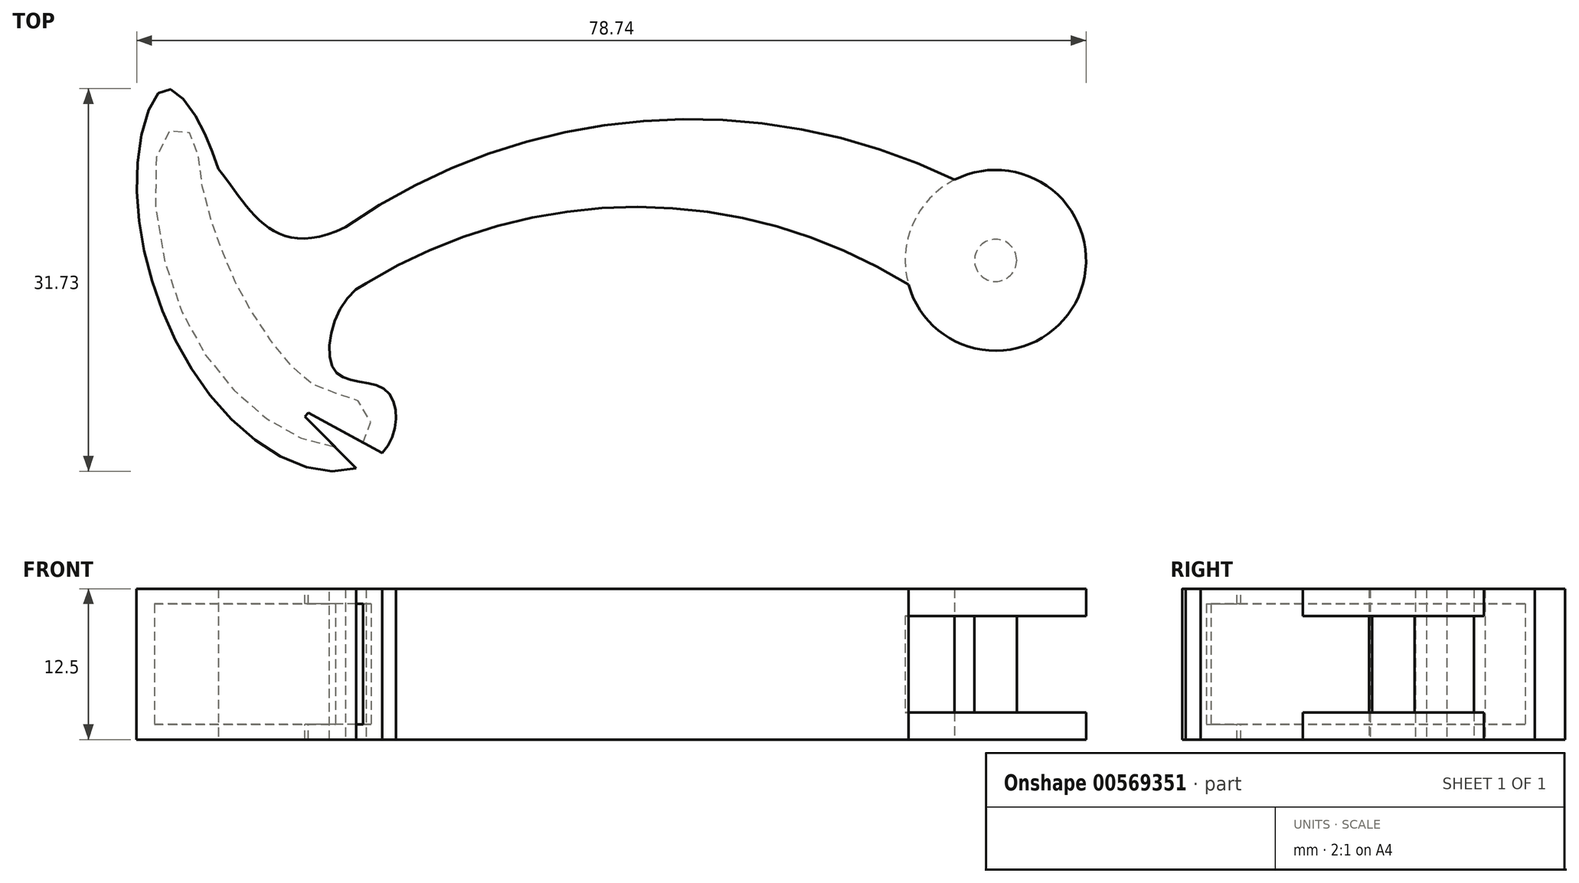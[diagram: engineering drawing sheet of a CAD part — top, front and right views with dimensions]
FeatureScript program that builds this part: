
annotation { "Feature Type Name" : "Feature", "Feature Type Description" : "" }
export const myFeature = defineFeature(function(context is Context, id is Id, definition is map)
    precondition{}
    {
        {
            var Q0;
            Q0=qCreatedBy(makeId("Top.planeOp"),FACE);
            var sketch = newSketch(context, id + "F0", { "sketchPlane" : qUnion([Q0])});
            skCircle(sketch, "E0", {"center": v(27.85, 26.85) * mm, "radius": 7.5 * mm});
            skArc(sketch, "E1", {"start": v(20.63, 24.85) * mm, "mid": v(-1.86, 31.28) * mm, "end": v(-24.37, 24.93) * mm});
            skArc(sketch, "E2.0", {"start": v(24.45, 33.54) * mm, "mid": v(-1.35, 38.42) * mm, "end": v(-26.08, 29.6) * mm});
            skFitSpline(sketch, "E3", {"points": [v(-26.08, 29.6) * mm, v(-36.61, 34.44) * mm], "startDerivative": vector(-18.17, -8.74) * mm, "endDerivative": vector(-7.9, 9.83) * mm});
            skFitSpline(sketch, "E4", {"points": [v(-36.61, 34.44) * mm, v(-38.36, 38.58) * mm, v(-40.96, 41.08) * mm, v(-43.15, 36.4) * mm, v(-42.32, 25.87) * mm, v(-36.61, 14.82) * mm, v(-27.83, 9.4) * mm, v(-22.42, 11.7) * mm, v(-22.83, 16.17) * mm, v(-27, 17.74) * mm, v(-24.37, 24.93) * mm], "startDerivative": vector(-16.63, 48.45) * mm, "endDerivative": vector(71.22, 29.47) * mm});
            skFitSpline(sketch, "E5", {"points": [v(-40.96, 37.36) * mm, v(-40.96, 26.4) * mm, v(-34.97, 15.74) * mm, v(-27.97, 11.52) * mm, v(-24.19, 12.14) * mm, v(-24.68, 14.93) * mm, v(-27.47, 15.98) * mm, v(-30.26, 17.78) * mm, v(-34.1, 22.99) * mm, v(-36.27, 27.57) * mm, v(-38.07, 33.7) * mm, v(-38.93, 37.36) * mm, v(-40.96, 37.36) * mm]});
            skSolve(sketch);
        }
        {
            var Q0;
            {var subQ1=sQuery(id+"F0.wireOp",EDGE,"E1");Q0=makeQuery(id+"F0.imprint","IMPRINT",FACE,{"disambiguationData":[TD([[makeQuery(id+"F0.imprint","IMPRINT",EDGE,{"derivedFrom":subQ1}),-1.0]])]});}
            var Q1;
            {var subQ0=sQuery(id+"F0.wireOp",EDGE,"E0");var subQ1=makeQuery(id+"F0.imprint","INTERSECT",VERTEX,{"derivedFrom":[subQ0,sQuery(id+"F0.wireOp",EDGE,"E1")]});Q1=makeQuery(id+"F0.imprint","IMPRINT",FACE,{"disambiguationData":[TD([[makeQuery(id+"F0.imprint","IMPRINT",EDGE,{"disambiguationData":[TD([[subQ1,1.0]])],"derivedFrom":subQ0}),1.0]])]});}
            var Q2;
            Q2=makeQuery(id+"F0.imprint","IMPRINT",FACE,{"disambiguationData":[TD([[makeQuery(id+"F0.imprint","IMPRINT",EDGE,{"derivedFrom":sQuery(id+"F0.wireOp",EDGE,"E5")}),1.0]])]});
            extrude(context, id + "F1", {"entities" : qUnion([Q0, Q1, Q2]), "endBound" : BoundingType.SYMMETRIC, "depth" : 12.5 * mm, "offsetDistance" : 25 * mm});
        }
        {
            var Q0;
            Q0=makeQuery(id+"F0.imprint","IMPRINT",FACE,{"disambiguationData":[TD([[makeQuery(id+"F0.imprint","IMPRINT",EDGE,{"derivedFrom":sQuery(id+"F0.wireOp",EDGE,"E5")}),1.0]])]});
            extrude(context, id + "F2", {"entities" : qUnion([Q0]), "operationType" : NewBodyOperationType.REMOVE, "endBound" : BoundingType.SYMMETRIC, "depth" : 10 * mm, "offsetDistance" : 25 * mm});
        }
        {
            var Q0;
            Q0=makeQuery(id+"F1.opExtrude","CAP_FACE",FACE,{"disambiguationData":[OSD([sQuery(id+"F0.wireOp",EDGE,"E0"),sQuery(id+"F0.wireOp",EDGE,"E1"),sQuery(id+"F0.wireOp",EDGE,"E2.0"),sQuery(id+"F0.wireOp",EDGE,"E3"),sQuery(id+"F0.wireOp",EDGE,"E4")])],"isStart":false});
            var sketch = newSketch(context, id + "F3", { "sketchPlane" : qUnion([Q0])});
            skLineSegment(sketch, "E6.bottom", {"start": v(-22.63, 10.66) * mm, "end": v(-29.14, 14.2) * mm});
            skLineSegment(sketch, "E6.top", {"start": v(-24.68, 9.13) * mm, "end": v(-29.43, 13.88) * mm});
            skLineSegment(sketch, "E6.left", {"start": v(-22.63, 10.66) * mm, "end": v(-24.68, 9.13) * mm});
            skLineSegment(sketch, "E6.right", {"start": v(-29.14, 14.2) * mm, "end": v(-29.43, 13.88) * mm});
            skSolve(sketch);
        }
        {
            var Q0;
            {var subQ1=sQuery(id+"F3.wireOp",EDGE,"E6.bottom");Q0=makeQuery(id+"F3.imprint","IMPRINT",FACE,{"disambiguationData":[TD([[makeQuery(id+"F3.imprint","IMPRINT",EDGE,{"derivedFrom":subQ1}),1.0]])]});}
            extrude(context, id + "F4", {"entities" : qUnion([Q0]), "operationType" : NewBodyOperationType.REMOVE, "endBound" : BoundingType.SYMMETRIC, "oppositeDirection" : true, "depth" : 25 * mm, "offsetDistance" : 25 * mm});
        }
        {
            var Q0;
            Q0=qCreatedBy(makeId("Top.planeOp"),FACE);
            var sketch = newSketch(context, id + "F5", { "sketchPlane" : qUnion([Q0])});
            skCircle(sketch, "E7", {"center": v(27.85, 26.85) * mm, "radius": 7.5 * mm});
            skCircle(sketch, "E8", {"center": v(27.85, 26.85) * mm, "radius": 1.75 * mm});
            skSolve(sketch);
        }
        {
            var Q0;
            {var subQ0=sQuery(id+"F5.wireOp",EDGE,"E7");Q0=makeQuery(id+"F5.imprint","IMPRINT",FACE,{"disambiguationData":[TD([[makeQuery(id+"F5.imprint","IMPRINT",EDGE,{"disambiguationData":[OD(0.0)],"derivedFrom":subQ0}),1.0]])]});}
            extrude(context, id + "F6", {"entities" : qUnion([Q0]), "operationType" : NewBodyOperationType.REMOVE, "endBound" : BoundingType.SYMMETRIC, "depth" : 8 * mm, "offsetDistance" : 25 * mm});
        }
    });
